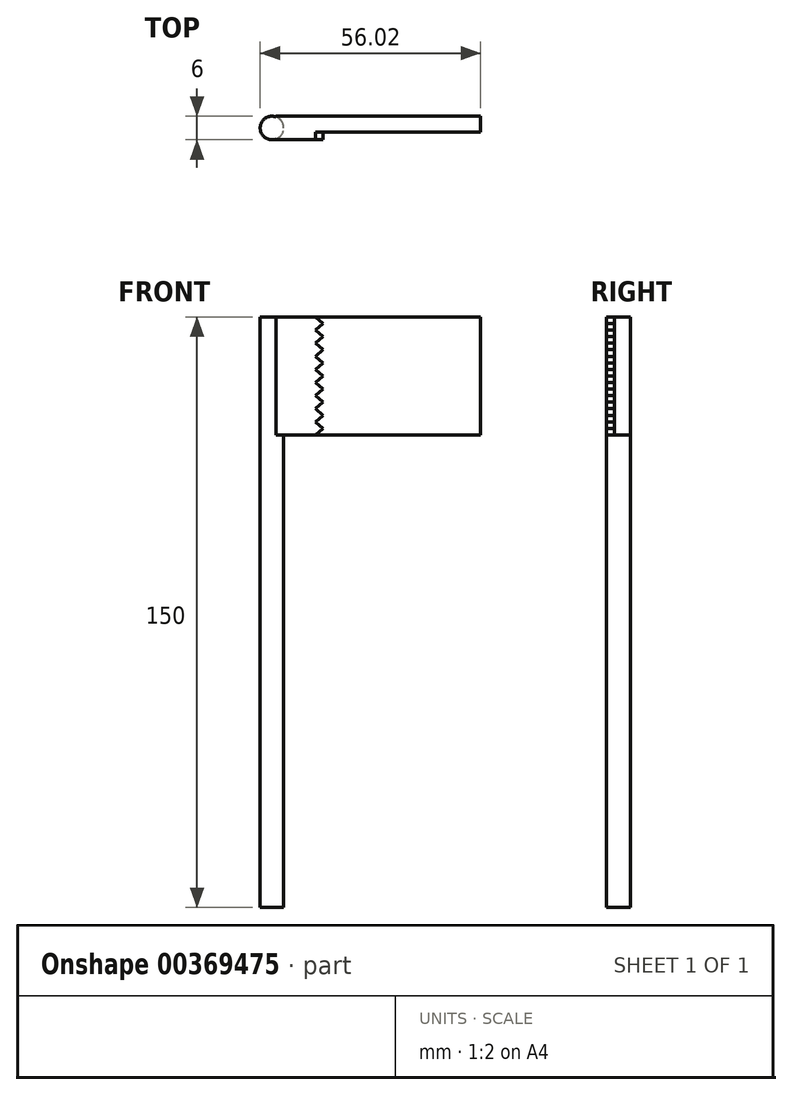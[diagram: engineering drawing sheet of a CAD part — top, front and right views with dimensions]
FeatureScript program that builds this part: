
annotation { "Feature Type Name" : "Feature", "Feature Type Description" : "" }
export const myFeature = defineFeature(function(context is Context, id is Id, definition is map)
    precondition{}
    {
        {
            var Q0;
            Q0=qCreatedBy(makeId("Top.planeOp"),FACE);
            var sketch = newSketch(context, id + "F0", { "sketchPlane" : qUnion([Q0])});
            skCircle(sketch, "E0", {"center": v(0, 0) * mm, "radius": 3 * mm});
            skSolve(sketch);
        }
        {
            var Q0;
            Q0 = qSketchRegion(id + "F0", true);
            extrude(context, id + "F1", {"entities" : qUnion([Q0]), "depth" : 150 * mm});
        }
        {
            var Q0;
            Q0=qCreatedBy(makeId("Front.planeOp"),FACE);
            var sketch = newSketch(context, id + "F2", { "sketchPlane" : qUnion([Q0])});
            skLineSegment(sketch, "E1.bottom", {"start": v(1.02, 150) * mm, "end": v(53.02, 150) * mm});
            skLineSegment(sketch, "E1.top", {"start": v(1.02, 120) * mm, "end": v(53.02, 120) * mm});
            skLineSegment(sketch, "E1.left", {"start": v(1.02, 150) * mm, "end": v(1.02, 120) * mm});
            skLineSegment(sketch, "E1.right", {"start": v(53.02, 150) * mm, "end": v(53.02, 120) * mm});
            skSolve(sketch);
        }
        {
            var Q0;
            Q0 = qSketchRegion(id + "F2", true);
            extrude(context, id + "F3", {"entities" : qUnion([Q0]), "operationType" : NewBodyOperationType.ADD, "endBound" : BoundingType.SYMMETRIC, "depth" : 6 * mm});
        }
        {
            var Q0;
            Q0=makeQuery(id+"F3.opExtrude","CAP_FACE",FACE,{"disambiguationData":[OSD([sQuery(id+"F2.wireOp",EDGE,"E1.bottom"),sQuery(id+"F2.wireOp",EDGE,"E1.top"),sQuery(id+"F2.wireOp",EDGE,"E1.left"),sQuery(id+"F2.wireOp",EDGE,"E1.right")])],"isStart":false});
            var sketch = newSketch(context, id + "F4", { "sketchPlane" : qUnion([Q0])});
            skLineSegment(sketch, "E2.bottom", {"start": v(53.02, 120) * mm, "end": v(1.02, 120) * mm});
            skLineSegment(sketch, "E2.top", {"start": v(53.02, 150) * mm, "end": v(1.02, 150) * mm});
            skLineSegment(sketch, "E2.left", {"start": v(53.02, 120) * mm, "end": v(53.02, 150) * mm});
            skLineSegment(sketch, "E2.right", {"start": v(1.02, 120) * mm, "end": v(1.02, 150) * mm});
            skPoint(sketch, "E2.middle", {"position": v(27.02, 135) * mm});
            skLineSegment(sketch, "E3", {"start": v(11.02, 150) * mm, "end": v(13.02, 148.32) * mm});
            skLineSegment(sketch, "E4", {"start": v(13.02, 148.32) * mm, "end": v(11.02, 146.67) * mm});
            skLineSegment(sketch, "E5.0.1.0", {"start": v(11.02, 146.67) * mm, "end": v(13.02, 144.99) * mm});
            skLineSegment(sketch, "E5.0.1.1", {"start": v(13.02, 144.99) * mm, "end": v(11.02, 143.33) * mm});
            skLineSegment(sketch, "E5.0.2.0", {"start": v(11.02, 143.33) * mm, "end": v(13.02, 141.66) * mm});
            skLineSegment(sketch, "E5.0.2.1", {"start": v(13.02, 141.66) * mm, "end": v(11.02, 140) * mm});
            skLineSegment(sketch, "E5.0.3.0", {"start": v(11.02, 140) * mm, "end": v(13.02, 138.32) * mm});
            skLineSegment(sketch, "E5.0.3.1", {"start": v(13.02, 138.32) * mm, "end": v(11.02, 136.67) * mm});
            skLineSegment(sketch, "E5.0.4.0", {"start": v(11.02, 136.67) * mm, "end": v(13.02, 134.99) * mm});
            skLineSegment(sketch, "E5.0.4.1", {"start": v(13.02, 134.99) * mm, "end": v(11.02, 133.33) * mm});
            skLineSegment(sketch, "E5.0.5.0", {"start": v(11.02, 133.33) * mm, "end": v(13.02, 131.66) * mm});
            skLineSegment(sketch, "E5.0.5.1", {"start": v(13.02, 131.66) * mm, "end": v(11.02, 130) * mm});
            skLineSegment(sketch, "E5.0.6.0", {"start": v(11.02, 130) * mm, "end": v(13.02, 128.32) * mm});
            skLineSegment(sketch, "E5.0.6.1", {"start": v(13.02, 128.32) * mm, "end": v(11.02, 126.67) * mm});
            skLineSegment(sketch, "E5.0.7.0", {"start": v(11.02, 126.67) * mm, "end": v(13.02, 124.99) * mm});
            skLineSegment(sketch, "E5.0.7.1", {"start": v(13.02, 124.99) * mm, "end": v(11.02, 123.33) * mm});
            skLineSegment(sketch, "E5.0.8.0", {"start": v(11.02, 123.33) * mm, "end": v(13.02, 121.66) * mm});
            skLineSegment(sketch, "E5.0.8.1", {"start": v(13.02, 121.66) * mm, "end": v(11.02, 120) * mm});
            skLineSegment(sketch, "E5.direction1", {"start": v(11.02, 150) * mm, "end": v(36.02, 150) * mm, "construction": true});
            skLineSegment(sketch, "E5.direction2", {"start": v(11.02, 150) * mm, "end": v(11.02, 146.67) * mm, "construction": true});
            skSolve(sketch);
        }
        {
            var Q0;
            {var subQ0=sQuery(id+"F4.wireOp",EDGE,"E2.left");Q0=makeQuery(id+"F4.imprint","IMPRINT",FACE,{"disambiguationData":[TD([[makeQuery(id+"F4.imprint","IMPRINT",EDGE,{"derivedFrom":subQ0}),-1.0]])]});}
            extrude(context, id + "F5", {"entities" : qUnion([Q0]), "operationType" : NewBodyOperationType.REMOVE, "oppositeDirection" : true, "depth" : 2 * mm});
        }
    });
